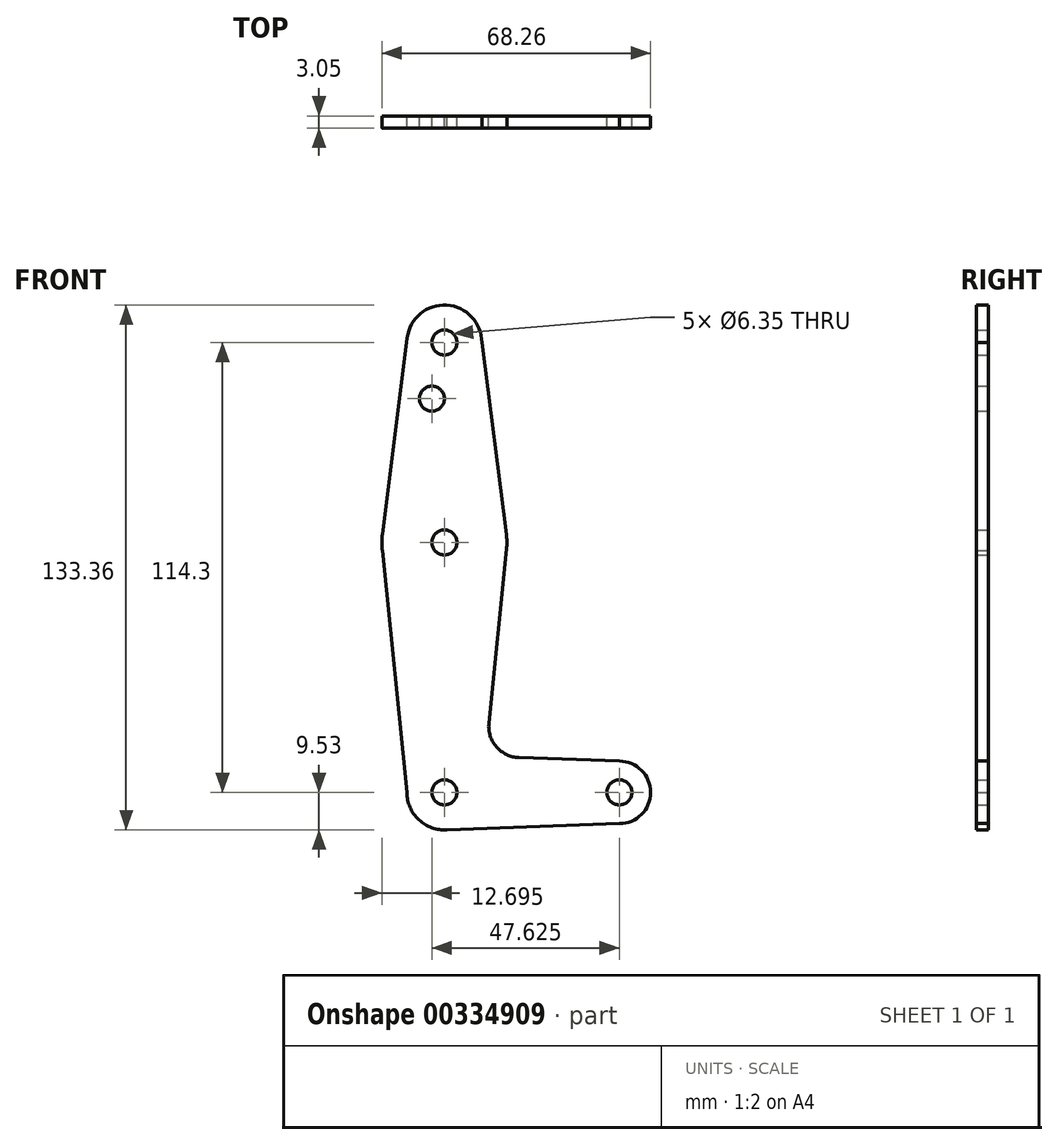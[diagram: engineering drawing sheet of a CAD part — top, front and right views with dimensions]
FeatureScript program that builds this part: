
annotation { "Feature Type Name" : "Feature", "Feature Type Description" : "" }
export const myFeature = defineFeature(function(context is Context, id is Id, definition is map)
    precondition{}
    {
        {
            var Q0;
            Q0=qCreatedBy(makeId("Front.planeOp"),FACE);
            var sketch = newSketch(context, id + "F0", { "sketchPlane" : qUnion([Q0])});
            skLineSegment(sketch, "E0", {"start": v(0, 0) * mm, "end": v(44.45, 0) * mm, "construction": true});
            skCircle(sketch, "E1", {"center": v(0, 114.3) * mm, "radius": 9.53 * mm});
            skCircle(sketch, "E2", {"center": v(0, 0) * mm, "radius": 9.53 * mm});
            skCircle(sketch, "E3", {"center": v(44.45, 0) * mm, "radius": 7.94 * mm});
            skLineSegment(sketch, "E4", {"start": v(44.45, -7.94) * mm, "end": v(0, -9.52) * mm});
            skLineSegment(sketch, "E5", {"start": v(0, 114.3) * mm, "end": v(0, 0) * mm, "construction": true});
            skCircle(sketch, "E6", {"center": v(0, 63.5) * mm, "radius": 15.88 * mm});
            skLineSegment(sketch, "E7", {"start": v(-15.75, 65.48) * mm, "end": v(-9.45, 115.5) * mm});
            skLineSegment(sketch, "E8", {"start": v(9.52, 114.3) * mm, "end": v(15.75, 65.5) * mm});
            skLineSegment(sketch, "E9", {"start": v(-15.75, 61.52) * mm, "end": v(-9.53, 0) * mm});
            skLineSegment(sketch, "E10", {"start": v(11.3, 17.6) * mm, "end": v(15.8, 61.9) * mm});
            skLineSegment(sketch, "E11", {"start": v(18.93, 8.85) * mm, "end": v(44.45, 7.94) * mm});
            skCircle(sketch, "E12", {"center": v(0, 114.3) * mm, "radius": 3.18 * mm});
            skCircle(sketch, "E13", {"center": v(0, 63.5) * mm, "radius": 3.18 * mm});
            skCircle(sketch, "E14", {"center": v(0, 0) * mm, "radius": 3.18 * mm});
            skCircle(sketch, "E15", {"center": v(44.45, 0) * mm, "radius": 3.18 * mm});
            skCircle(sketch, "E16", {"center": v(-3.17, 100.03) * mm, "radius": 3.18 * mm});
            skPoint(sketch, "E17.newPointB", {"position": v(0, 9.53) * mm});
            skArc(sketch, "E17.filletArc", {"start": v(11.3, 17.6) * mm, "mid": v(13.22, 11.57) * mm, "end": v(18.93, 8.85) * mm});
            skSolve(sketch);
        }
        {
            var Q0;
            Q0 = qSketchRegion(id + "F0", true);
            extrude(context, id + "F1", {"entities" : qUnion([Q0]), "depth" : 3.05 * mm});
        }
        {
            var Q0;
            Q0 = qSketchRegion(id + "F0", true);
            extrude(context, id + "F2", {"entities" : qUnion([Q0]), "operationType" : NewBodyOperationType.ADD, "depth" : 3.05 * mm});
        }
    });
